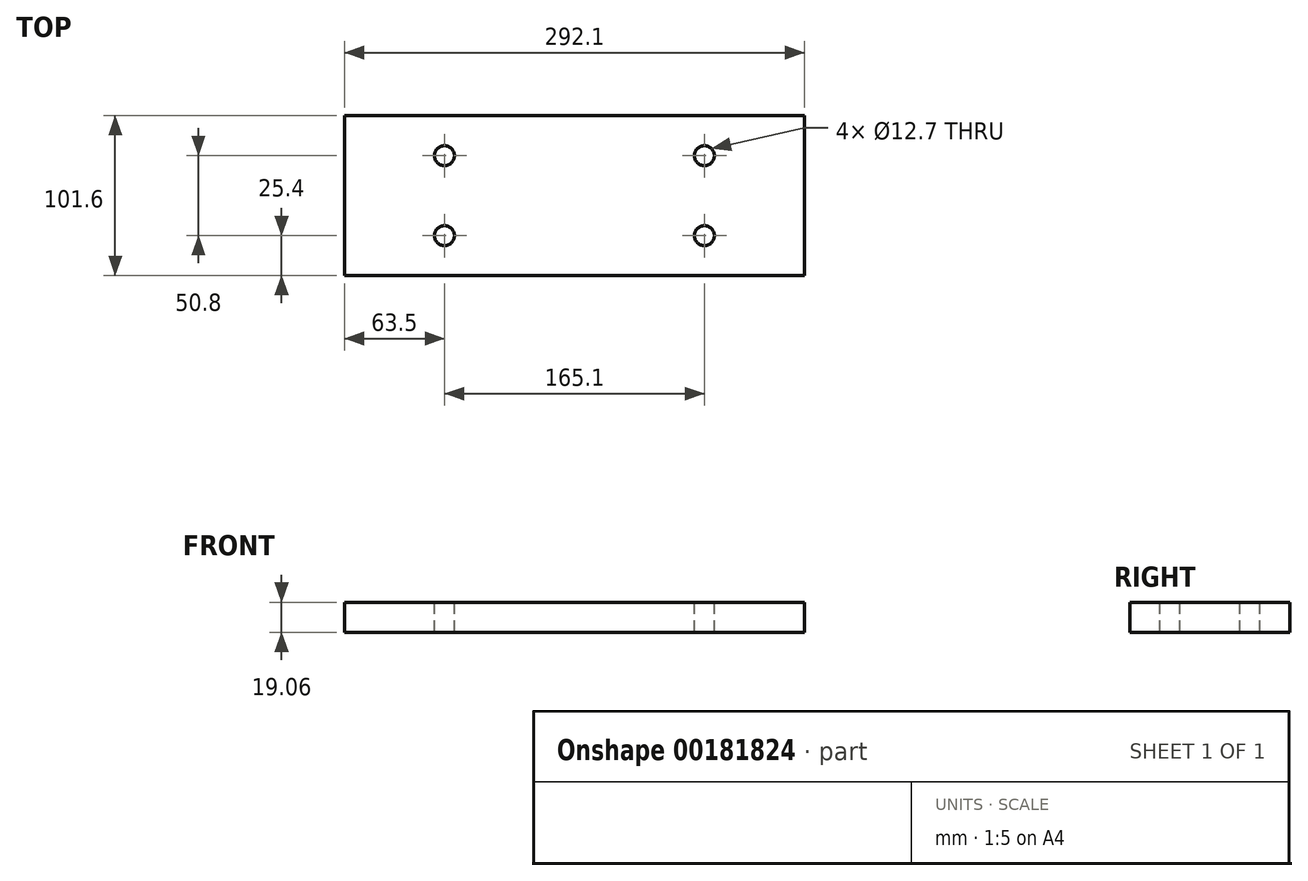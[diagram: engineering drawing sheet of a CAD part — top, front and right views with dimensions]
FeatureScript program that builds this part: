
annotation { "Feature Type Name" : "Feature", "Feature Type Description" : "" }
export const myFeature = defineFeature(function(context is Context, id is Id, definition is map)
    precondition{}
    {
        {
            var Q0;
            Q0=qCreatedBy(makeId("Top.planeOp"),FACE);
            var sketch = newSketch(context, id + "F0", { "sketchPlane" : qUnion([Q0])});
            skLineSegment(sketch, "E0.bottom", {"start": v(146.05, 50.8) * mm, "end": v(-146.05, 50.8) * mm});
            skLineSegment(sketch, "E0.top", {"start": v(146.05, -50.8) * mm, "end": v(-146.05, -50.8) * mm});
            skLineSegment(sketch, "E0.left", {"start": v(146.05, 50.8) * mm, "end": v(146.05, -50.8) * mm});
            skLineSegment(sketch, "E0.right", {"start": v(-146.05, 50.8) * mm, "end": v(-146.05, -50.8) * mm});
            skPoint(sketch, "E0.middle", {"position": v(0, 0) * mm});
            skSolve(sketch);
        }
        {
            var Q0;
            Q0 = qSketchRegion(id + "F0", true);
            extrude(context, id + "F1", {"entities" : qUnion([Q0]), "endBound" : BoundingType.SYMMETRIC, "depth" : 19.05 * mm});
        }
        {
            var Q0;
            Q0=makeQuery(id+"F1.opExtrude","CAP_FACE",FACE,{"disambiguationData":[OSD([sQuery(id+"F0.wireOp",EDGE,"E0.bottom"),sQuery(id+"F0.wireOp",EDGE,"E0.top"),sQuery(id+"F0.wireOp",EDGE,"E0.left"),sQuery(id+"F0.wireOp",EDGE,"E0.right")])],"isStart":false});
            var sketch = newSketch(context, id + "F2", { "sketchPlane" : qUnion([Q0])});
            skCircle(sketch, "E1", {"center": v(-82.55, 25.4) * mm, "radius": 6.35 * mm});
            skCircle(sketch, "E2", {"center": v(82.55, 25.4) * mm, "radius": 6.35 * mm});
            skCircle(sketch, "E3", {"center": v(82.55, -25.4) * mm, "radius": 6.35 * mm});
            skCircle(sketch, "E4", {"center": v(-82.55, -25.4) * mm, "radius": 6.35 * mm});
            skSolve(sketch);
        }
        {
            var Q0;
            Q0 = qSketchRegion(id + "F2", true);
            extrude(context, id + "F3", {"entities" : qUnion([Q0]), "operationType" : NewBodyOperationType.REMOVE, "endBound" : BoundingType.SYMMETRIC, "oppositeDirection" : true, "depth" : 127 * mm});
        }
    });
